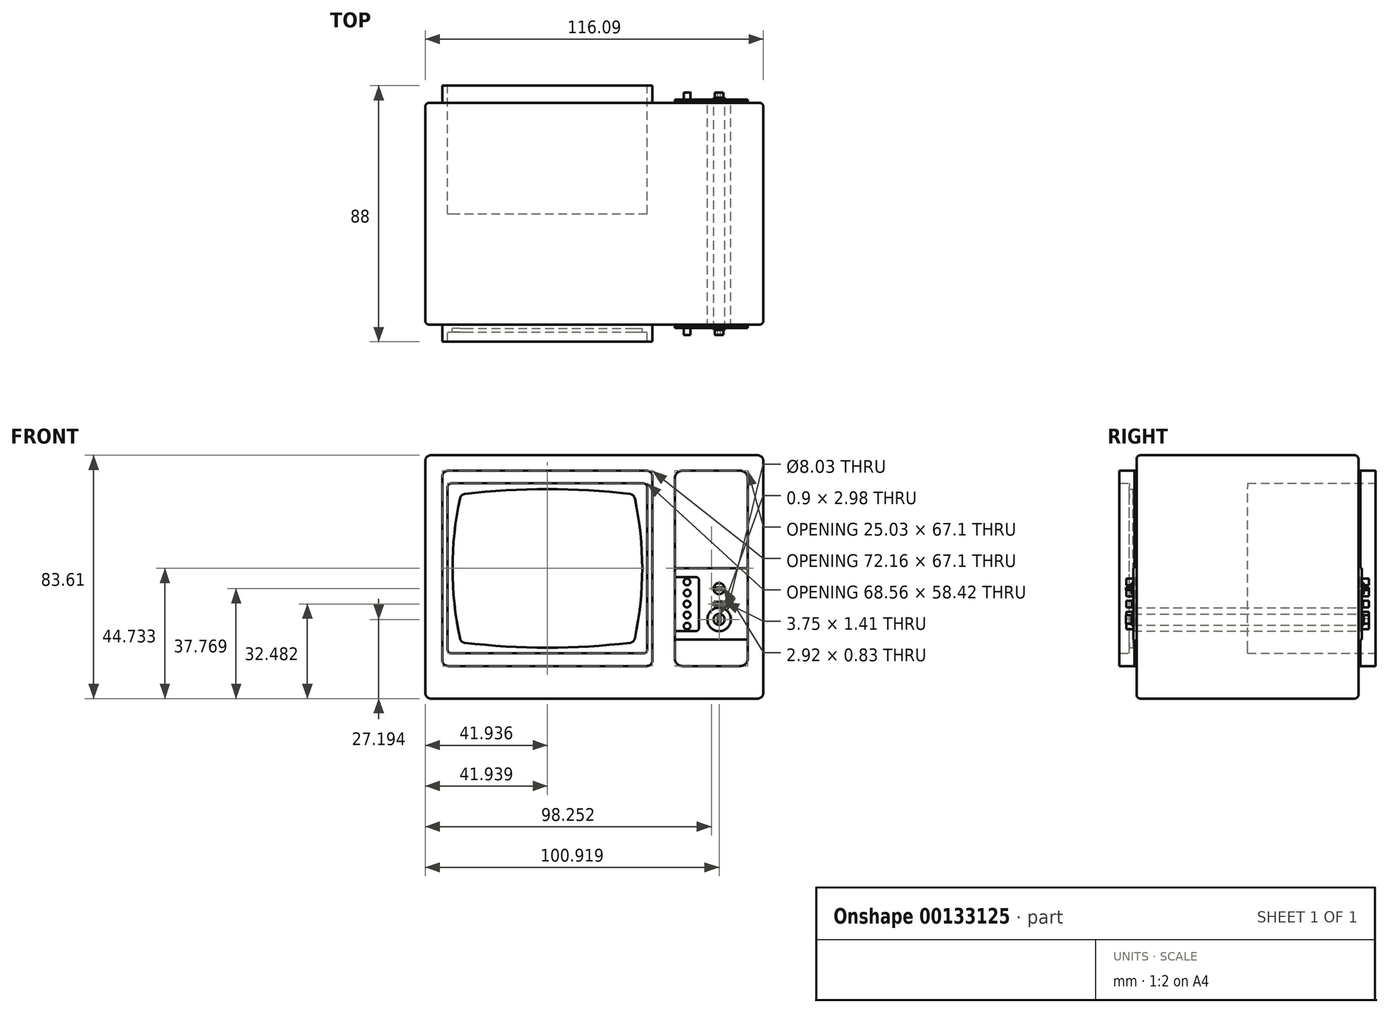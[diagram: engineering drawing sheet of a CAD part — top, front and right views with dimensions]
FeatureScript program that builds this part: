
annotation { "Feature Type Name" : "Feature", "Feature Type Description" : "" }
export const myFeature = defineFeature(function(context is Context, id is Id, definition is map)
    precondition{}
    {
        {
            var Q0;
            Q0=qCreatedBy(makeId("Front.planeOp"),FACE);
            var sketch = newSketch(context, id + "F0", { "sketchPlane" : qUnion([Q0])});
            skLineSegment(sketch, "E0.bottom", {"start": v(-54.54, 43.27) * mm, "end": v(57.74, 43.27) * mm});
            skLineSegment(sketch, "E0.top", {"start": v(-54.54, -40.34) * mm, "end": v(57.74, -40.34) * mm});
            skLineSegment(sketch, "E0.left", {"start": v(-56.45, 41.36) * mm, "end": v(-56.45, -38.43) * mm});
            skLineSegment(sketch, "E0.right", {"start": v(59.64, 41.36) * mm, "end": v(59.64, -38.43) * mm});
            skLineSegment(sketch, "E1.bottom", {"start": v(-48.68, 37.94) * mm, "end": v(19.66, 37.94) * mm});
            skLineSegment(sketch, "E1.top", {"start": v(-48.68, -29.16) * mm, "end": v(19.66, -29.16) * mm});
            skLineSegment(sketch, "E1.left", {"start": v(-50.59, 36.04) * mm, "end": v(-50.59, -27.25) * mm});
            skLineSegment(sketch, "E1.right", {"start": v(21.57, 36.04) * mm, "end": v(21.57, -27.25) * mm});
            skLineSegment(sketch, "E2.bottom", {"start": v(31.83, 37.94) * mm, "end": v(51.78, 37.94) * mm});
            skLineSegment(sketch, "E2.left", {"start": v(29.29, 35.4) * mm, "end": v(29.29, -26.62) * mm});
            skLineSegment(sketch, "E2.right", {"start": v(54.32, 35.4) * mm, "end": v(54.32, -26.62) * mm});
            skPoint(sketch, "E3.visualSharp", {"position": v(54.32, 37.94) * mm});
            skArc(sketch, "E3.filletArc", {"start": v(54.32, 35.4) * mm, "mid": v(53.57, 37.2) * mm, "end": v(51.78, 37.94) * mm});
            skPoint(sketch, "E4.visualSharp", {"position": v(54.32, -29.16) * mm});
            skArc(sketch, "E4.filletArc", {"start": v(51.78, -29.16) * mm, "mid": v(53.57, -28.41) * mm, "end": v(54.32, -26.62) * mm});
            skPoint(sketch, "E5.visualSharp", {"position": v(29.29, 37.94) * mm});
            skArc(sketch, "E5.filletArc", {"start": v(31.83, 37.94) * mm, "mid": v(30.03, 37.2) * mm, "end": v(29.29, 35.4) * mm});
            skPoint(sketch, "E6.visualSharp", {"position": v(29.29, -29.16) * mm});
            skArc(sketch, "E6.filletArc", {"start": v(29.29, -26.62) * mm, "mid": v(30.03, -28.41) * mm, "end": v(31.83, -29.16) * mm});
            skLineSegment(sketch, "E7", {"start": v(29.29, 4.4) * mm, "end": v(54.32, 4.4) * mm});
            skLineSegment(sketch, "E8", {"start": v(29.29, -20.1) * mm, "end": v(54.32, -20.1) * mm});
            skLineSegment(sketch, "E9", {"start": v(29.29, 1.46) * mm, "end": v(34.62, 1.46) * mm});
            skLineSegment(sketch, "E10", {"start": v(29.29, -17.18) * mm, "end": v(34.62, -17.18) * mm});
            skCircle(sketch, "E11", {"center": v(44.47, -2.57) * mm, "radius": 4.02 * mm});
            skCircle(sketch, "E12.MirrorC", {"center": v(44.47, -13.15) * mm, "radius": 4.02 * mm});
            skLineSegment(sketch, "E13", {"start": v(34.62, 1.46) * mm, "end": v(36.34, 1.46) * mm});
            skLineSegment(sketch, "E14", {"start": v(37.6, 0.2) * mm, "end": v(37.6, -15.92) * mm});
            skLineSegment(sketch, "E15", {"start": v(36.34, -17.18) * mm, "end": v(34.62, -17.18) * mm});
            skLineSegment(sketch, "E16", {"start": v(29.29, 1.46) * mm, "end": v(29.29, -17.18) * mm});
            skLineSegment(sketch, "E17", {"start": v(29.29, -7.86) * mm, "end": v(29.29, 1.46) * mm});
            skLineSegment(sketch, "E18", {"start": v(29.29, -7.86) * mm, "end": v(29.29, -17.18) * mm});
            skLineSegment(sketch, "E19.bottom", {"start": v(46.35, -7.15) * mm, "end": v(42.6, -7.15) * mm});
            skLineSegment(sketch, "E19.top", {"start": v(46.35, -8.56) * mm, "end": v(42.6, -8.56) * mm});
            skLineSegment(sketch, "E19.left", {"start": v(46.35, -7.15) * mm, "end": v(46.35, -8.56) * mm});
            skLineSegment(sketch, "E19.right", {"start": v(42.6, -7.15) * mm, "end": v(42.6, -8.56) * mm});
            skPoint(sketch, "E19.middle", {"position": v(44.47, -7.86) * mm});
            skCircle(sketch, "E20", {"center": v(33.44, -7.86) * mm, "radius": 1.14 * mm});
            skCircle(sketch, "E21", {"center": v(33.44, -0.3) * mm, "radius": 1.14 * mm});
            skCircle(sketch, "E22", {"center": v(33.47, -15.42) * mm, "radius": 1.14 * mm});
            skCircle(sketch, "E23", {"center": v(33.52, -4.08) * mm, "radius": 1.15 * mm});
            skCircle(sketch, "E24", {"center": v(33.47, -11.64) * mm, "radius": 1.15 * mm});
            skPoint(sketch, "E25.endSnap0", {"position": v(-50.59, 4.4) * mm});
            skArc(sketch, "E26", {"start": v(13.87, 29.96) * mm, "mid": v(-14.51, 31.63) * mm, "end": v(-42.9, 29.96) * mm});
            skArc(sketch, "E27", {"start": v(-42.9, -21.17) * mm, "mid": v(-14.51, -22.84) * mm, "end": v(13.87, -21.17) * mm});
            skArc(sketch, "E28", {"start": v(-44.53, 28.47) * mm, "mid": v(-47.1, 4.4) * mm, "end": v(-44.53, -19.68) * mm});
            skArc(sketch, "E29", {"start": v(15.51, -19.68) * mm, "mid": v(18.07, 4.4) * mm, "end": v(15.51, 28.47) * mm});
            skPoint(sketch, "E30.visualSharp", {"position": v(21.57, 37.94) * mm});
            skArc(sketch, "E30.filletArc", {"start": v(21.57, 36.04) * mm, "mid": v(21, 37.38) * mm, "end": v(19.66, 37.94) * mm});
            skPoint(sketch, "E31.visualSharp", {"position": v(-50.59, 37.94) * mm});
            skArc(sketch, "E31.filletArc", {"start": v(-48.68, 37.94) * mm, "mid": v(-50.03, 37.38) * mm, "end": v(-50.59, 36.04) * mm});
            skPoint(sketch, "E32.visualSharp", {"position": v(-50.59, -29.16) * mm});
            skArc(sketch, "E32.filletArc", {"start": v(-50.59, -27.25) * mm, "mid": v(-50.03, -28.6) * mm, "end": v(-48.68, -29.16) * mm});
            skPoint(sketch, "E33.visualSharp", {"position": v(21.57, -29.16) * mm});
            skArc(sketch, "E33.filletArc", {"start": v(19.66, -29.16) * mm, "mid": v(21, -28.6) * mm, "end": v(21.57, -27.25) * mm});
            skPoint(sketch, "E34.visualSharp", {"position": v(-44.24, 29.8) * mm});
            skArc(sketch, "E34.filletArc", {"start": v(-42.9, 29.96) * mm, "mid": v(-43.95, 29.47) * mm, "end": v(-44.53, 28.47) * mm});
            skPoint(sketch, "E35.visualSharp", {"position": v(15.22, 29.8) * mm});
            skArc(sketch, "E35.filletArc", {"start": v(15.51, 28.47) * mm, "mid": v(14.93, 29.47) * mm, "end": v(13.87, 29.96) * mm});
            skPoint(sketch, "E36.visualSharp", {"position": v(15.22, -21) * mm});
            skArc(sketch, "E36.filletArc", {"start": v(13.87, -21.17) * mm, "mid": v(14.93, -20.69) * mm, "end": v(15.51, -19.68) * mm});
            skPoint(sketch, "E37.visualSharp", {"position": v(-44.24, -21) * mm});
            skArc(sketch, "E37.filletArc", {"start": v(-44.53, -19.68) * mm, "mid": v(-43.95, -20.69) * mm, "end": v(-42.9, -21.17) * mm});
            skPoint(sketch, "E38.visualSharp", {"position": v(-56.45, 43.27) * mm});
            skArc(sketch, "E38.filletArc", {"start": v(-54.54, 43.27) * mm, "mid": v(-55.89, 42.7) * mm, "end": v(-56.45, 41.36) * mm});
            skPoint(sketch, "E39.visualSharp", {"position": v(-56.45, -40.34) * mm});
            skArc(sketch, "E39.filletArc", {"start": v(-56.45, -38.43) * mm, "mid": v(-55.89, -39.78) * mm, "end": v(-54.54, -40.34) * mm});
            skPoint(sketch, "E40.visualSharp", {"position": v(59.64, -40.34) * mm});
            skArc(sketch, "E40.filletArc", {"start": v(57.74, -40.34) * mm, "mid": v(59.08, -39.78) * mm, "end": v(59.64, -38.43) * mm});
            skPoint(sketch, "E41.visualSharp", {"position": v(59.64, 43.27) * mm});
            skArc(sketch, "E41.filletArc", {"start": v(59.64, 41.36) * mm, "mid": v(59.08, 42.7) * mm, "end": v(57.74, 43.27) * mm});
            skPoint(sketch, "E42.visualSharp", {"position": v(37.6, -17.18) * mm});
            skArc(sketch, "E42.filletArc", {"start": v(36.34, -17.18) * mm, "mid": v(37.23, -16.81) * mm, "end": v(37.6, -15.92) * mm});
            skPoint(sketch, "E43.visualSharp", {"position": v(37.6, 1.46) * mm});
            skArc(sketch, "E43.filletArc", {"start": v(37.6, 0.2) * mm, "mid": v(37.23, 1.1) * mm, "end": v(36.34, 1.46) * mm});
            skLineSegment(sketch, "E44", {"start": v(-50.59, 4.4) * mm, "end": v(-47, 4.4) * mm});
            skLineSegment(sketch, "E45", {"start": v(-48.8, 4.4) * mm, "end": v(-48.8, -23.56) * mm});
            skLineSegment(sketch, "E46", {"start": v(-48.8, 4.4) * mm, "end": v(-48.8, 32.35) * mm});
            skLineSegment(sketch, "E47", {"start": v(21.57, 4.4) * mm, "end": v(17.96, 4.4) * mm});
            skLineSegment(sketch, "E48", {"start": v(19.76, 4.4) * mm, "end": v(19.76, 32.35) * mm});
            skLineSegment(sketch, "E49", {"start": v(19.76, 4.4) * mm, "end": v(19.76, -23.56) * mm});
            skLineSegment(sketch, "E50", {"start": v(-47.54, 33.6) * mm, "end": v(18.5, 33.6) * mm});
            skLineSegment(sketch, "E51", {"start": v(-47.54, -24.82) * mm, "end": v(18.5, -24.82) * mm});
            skPoint(sketch, "E52.visualSharp", {"position": v(-48.8, 33.6) * mm});
            skArc(sketch, "E52.filletArc", {"start": v(-47.54, 33.6) * mm, "mid": v(-48.42, 33.24) * mm, "end": v(-48.8, 32.35) * mm});
            skPoint(sketch, "E53.visualSharp", {"position": v(19.76, 33.6) * mm});
            skArc(sketch, "E53.filletArc", {"start": v(19.76, 32.35) * mm, "mid": v(19.4, 33.24) * mm, "end": v(18.5, 33.6) * mm});
            skPoint(sketch, "E54.visualSharp", {"position": v(19.76, -24.82) * mm});
            skArc(sketch, "E54.filletArc", {"start": v(18.5, -24.82) * mm, "mid": v(19.4, -24.45) * mm, "end": v(19.76, -23.56) * mm});
            skPoint(sketch, "E55.visualSharp", {"position": v(-48.8, -24.82) * mm});
            skArc(sketch, "E55.filletArc", {"start": v(-48.8, -23.56) * mm, "mid": v(-48.42, -24.45) * mm, "end": v(-47.54, -24.82) * mm});
            skLineSegment(sketch, "E56", {"start": v(51.78, -29.16) * mm, "end": v(31.83, -29.16) * mm});
            skCircle(sketch, "E57", {"center": v(44.47, -2.57) * mm, "radius": 1.9 * mm});
            skCircle(sketch, "E58", {"center": v(44.47, -13.15) * mm, "radius": 1.9 * mm});
            skLineSegment(sketch, "E59.bottom", {"start": v(44.02, -11.65) * mm, "end": v(44.92, -11.65) * mm});
            skLineSegment(sketch, "E59.top", {"start": v(44.02, -14.64) * mm, "end": v(44.92, -14.64) * mm});
            skLineSegment(sketch, "E59.left", {"start": v(44.02, -11.65) * mm, "end": v(44.02, -14.64) * mm});
            skLineSegment(sketch, "E59.right", {"start": v(44.92, -11.65) * mm, "end": v(44.92, -14.64) * mm});
            skLineSegment(sketch, "E60.bottom", {"start": v(45.93, -2.15) * mm, "end": v(43, -2.15) * mm});
            skLineSegment(sketch, "E60.top", {"start": v(45.93, -2.99) * mm, "end": v(43, -2.99) * mm});
            skLineSegment(sketch, "E60.left", {"start": v(45.93, -2.15) * mm, "end": v(45.93, -2.99) * mm});
            skLineSegment(sketch, "E60.right", {"start": v(43, -2.15) * mm, "end": v(43, -2.99) * mm});
            skSolve(sketch);
        }
        {
            var Q0;
            Q0 = qSketchRegion(id + "F0", true);
            extrude(context, id + "F1", {"entities" : qUnion([Q0]), "endBound" : BoundingType.SYMMETRIC, "depth" : 76.2 * mm});
        }
        {
            var Q0;
            Q0=makeQuery(id+"F0.imprint","IMPRINT",FACE,{"disambiguationData":[TD([[makeQuery(id+"F0.imprint","IMPRINT",EDGE,{"derivedFrom":sQuery(id+"F0.wireOp",EDGE,"E1.bottom")}),-1.0]])]});
            var Q1;
            Q1=makeQuery(id+"F0.imprint","IMPRINT",FACE,{"disambiguationData":[TD([[makeQuery(id+"F0.imprint","IMPRINT",EDGE,{"derivedFrom":sQuery(id+"F0.wireOp",EDGE,"E1.top")}),1.0]])]});
            extrude(context, id + "F2", {"entities" : qUnion([Q0, Q1]), "operationType" : NewBodyOperationType.ADD, "endBound" : BoundingType.SYMMETRIC, "depth" : 88 * mm});
        }
        {
            var Q0;
            Q0=makeQuery(id+"F0.imprint","IMPRINT",FACE,{"disambiguationData":[TD([[makeQuery(id+"F0.imprint","IMPRINT",EDGE,{"derivedFrom":sQuery(id+"F0.wireOp",EDGE,"E26")}),-1.0]])]});
            var Q1;
            Q1=makeQuery(id+"F0.imprint","IMPRINT",FACE,{"disambiguationData":[TD([[makeQuery(id+"F0.imprint","IMPRINT",EDGE,{"derivedFrom":sQuery(id+"F0.wireOp",EDGE,"E27")}),-1.0]])]});
            extrude(context, id + "F3", {"entities" : qUnion([Q0, Q1]), "operationType" : NewBodyOperationType.ADD, "depth" : 40.64 * mm});
        }
        {
            var Q0;
            Q0=makeQuery(id+"F0.imprint","IMPRINT",FACE,{"disambiguationData":[TD([[makeQuery(id+"F0.imprint","IMPRINT",EDGE,{"derivedFrom":sQuery(id+"F0.wireOp",EDGE,"E26")}),1.0]])]});
            extrude(context, id + "F4", {"entities" : qUnion([Q0]), "operationType" : NewBodyOperationType.ADD, "depth" : 39.37 * mm});
        }
        {
            var Q0;
            Q0=makeQuery(id+"F0.imprint","IMPRINT",FACE,{"disambiguationData":[TD([[makeQuery(id+"F0.imprint","IMPRINT",EDGE,{"derivedFrom":sQuery(id+"F0.wireOp",EDGE,"E2.bottom")}),-1.0]])]});
            var Q1;
            {var subQ1=sQuery(id+"F0.wireOp",EDGE,"E4.filletArc");Q1=makeQuery(id+"F0.imprint","IMPRINT",FACE,{"disambiguationData":[TD([[makeQuery(id+"F0.imprint","IMPRINT",EDGE,{"derivedFrom":subQ1}),1.0]])]});}
            var Q2;
            {var subQ4=sQuery(id+"F0.wireOp",EDGE,"E7");Q2=makeQuery(id+"F0.imprint","IMPRINT",FACE,{"disambiguationData":[TD([[makeQuery(id+"F0.imprint","IMPRINT",EDGE,{"derivedFrom":subQ4}),-1.0]])]});}
            var Q3;
            Q3=makeQuery(id+"F0.imprint","IMPRINT",FACE,{"disambiguationData":[TD([[makeQuery(id+"F0.imprint","IMPRINT",EDGE,{"derivedFrom":sQuery(id+"F0.wireOp",EDGE,"E9")}),-1.0]])]});
            extrude(context, id + "F5", {"entities" : qUnion([Q0, Q1, Q2, Q3]), "operationType" : NewBodyOperationType.ADD, "endBound" : BoundingType.SYMMETRIC, "depth" : 77.6 * mm});
        }
        {
            var Q0;
            Q0=makeQuery(id+"F0.imprint","IMPRINT",FACE,{"disambiguationData":[TD([[makeQuery(id+"F0.imprint","IMPRINT",EDGE,{"derivedFrom":sQuery(id+"F0.wireOp",EDGE,"E19.bottom")}),1.0]])]});
            extrude(context, id + "F6", {"entities" : qUnion([Q0]), "operationType" : NewBodyOperationType.ADD, "endBound" : BoundingType.SYMMETRIC, "depth" : 79.28 * mm});
        }
        {
            var Q0;
            Q0=makeQuery(id+"F0.imprint","IMPRINT",FACE,{"disambiguationData":[TD([[makeQuery(id+"F0.imprint","IMPRINT",EDGE,{"derivedFrom":sQuery(id+"F0.wireOp",EDGE,"E21")}),1.0]])]});
            var Q1;
            Q1=makeQuery(id+"F0.imprint","IMPRINT",FACE,{"disambiguationData":[TD([[makeQuery(id+"F0.imprint","IMPRINT",EDGE,{"derivedFrom":sQuery(id+"F0.wireOp",EDGE,"E23")}),1.0]])]});
            var Q2;
            Q2=makeQuery(id+"F0.imprint","IMPRINT",FACE,{"disambiguationData":[TD([[makeQuery(id+"F0.imprint","IMPRINT",EDGE,{"derivedFrom":sQuery(id+"F0.wireOp",EDGE,"E20")}),1.0]])]});
            var Q3;
            Q3=makeQuery(id+"F0.imprint","IMPRINT",FACE,{"disambiguationData":[TD([[makeQuery(id+"F0.imprint","IMPRINT",EDGE,{"derivedFrom":sQuery(id+"F0.wireOp",EDGE,"E24")}),1.0]])]});
            var Q4;
            Q4=makeQuery(id+"F0.imprint","IMPRINT",FACE,{"disambiguationData":[TD([[makeQuery(id+"F0.imprint","IMPRINT",EDGE,{"derivedFrom":sQuery(id+"F0.wireOp",EDGE,"E22")}),1.0]])]});
            extrude(context, id + "F7", {"entities" : qUnion([Q0, Q1, Q2, Q3, Q4]), "operationType" : NewBodyOperationType.ADD, "endBound" : BoundingType.SYMMETRIC, "depth" : 83.3 * mm});
        }
        {
            var Q0;
            Q0=makeQuery(id+"F0.imprint","IMPRINT",FACE,{"disambiguationData":[TD([[makeQuery(id+"F0.imprint","IMPRINT",EDGE,{"derivedFrom":sQuery(id+"F0.wireOp",EDGE,"E11")}),1.0]])]});
            var Q1;
            Q1=makeQuery(id+"F0.imprint","IMPRINT",FACE,{"disambiguationData":[TD([[makeQuery(id+"F0.imprint","IMPRINT",EDGE,{"derivedFrom":sQuery(id+"F0.wireOp",EDGE,"E12.MirrorC")}),-1.0]])]});
            extrude(context, id + "F8", {"entities" : qUnion([Q0, Q1]), "operationType" : NewBodyOperationType.ADD, "endBound" : BoundingType.SYMMETRIC, "depth" : 78.49 * mm});
        }
        {
            var Q0;
            Q0=makeQuery(id+"F0.imprint","IMPRINT",FACE,{"disambiguationData":[TD([[makeQuery(id+"F0.imprint","IMPRINT",EDGE,{"derivedFrom":sQuery(id+"F0.wireOp",EDGE,"E57")}),1.0]])]});
            var Q1;
            Q1=makeQuery(id+"F0.imprint","IMPRINT",FACE,{"disambiguationData":[TD([[makeQuery(id+"F0.imprint","IMPRINT",EDGE,{"derivedFrom":sQuery(id+"F0.wireOp",EDGE,"E58")}),1.0]])]});
            extrude(context, id + "F9", {"entities" : qUnion([Q0, Q1]), "operationType" : NewBodyOperationType.ADD, "endBound" : BoundingType.SYMMETRIC, "depth" : 79.78 * mm});
        }
        {
            var Q0;
            Q0=makeQuery(id+"F0.imprint","IMPRINT",FACE,{"disambiguationData":[TD([[makeQuery(id+"F0.imprint","IMPRINT",EDGE,{"derivedFrom":sQuery(id+"F0.wireOp",EDGE,"E59.bottom")}),-1.0]])]});
            var Q1;
            Q1=makeQuery(id+"F0.imprint","IMPRINT",FACE,{"disambiguationData":[TD([[makeQuery(id+"F0.imprint","IMPRINT",EDGE,{"derivedFrom":sQuery(id+"F0.wireOp",EDGE,"E60.bottom")}),1.0]])]});
            extrude(context, id + "F10", {"entities" : qUnion([Q0, Q1]), "operationType" : NewBodyOperationType.ADD, "endBound" : BoundingType.SYMMETRIC, "depth" : 83.33 * mm});
        }
        {
            var Q0;
            Q0=makeQuery(id+"F1.opExtrude","SWEPT_FACE",FACE,{"disambiguationData":[OSD([sQuery(id+"F0.wireOp",EDGE,"E0.bottom")])]});
            var Q1;
            Q1=makeQuery(id+"F1.opExtrude","SWEPT_FACE",FACE,{"disambiguationData":[OSD([sQuery(id+"F0.wireOp",EDGE,"E0.right")])]});
            var Q2;
            Q2=makeQuery(id+"F1.opExtrude","SWEPT_FACE",FACE,{"disambiguationData":[OSD([sQuery(id+"F0.wireOp",EDGE,"E41.filletArc")])]});
            var Q3;
            Q3=makeQuery(id+"F1.opExtrude","SWEPT_FACE",FACE,{"disambiguationData":[OSD([sQuery(id+"F0.wireOp",EDGE,"E0.top")])]});
            var Q4;
            Q4=makeQuery(id+"F1.opExtrude","SWEPT_FACE",FACE,{"disambiguationData":[OSD([sQuery(id+"F0.wireOp",EDGE,"E40.filletArc")])]});
            var Q5;
            Q5=makeQuery(id+"F1.opExtrude","SWEPT_FACE",FACE,{"disambiguationData":[OSD([sQuery(id+"F0.wireOp",EDGE,"E0.left")])]});
            var Q6;
            Q6=makeQuery(id+"F1.opExtrude","SWEPT_FACE",FACE,{"disambiguationData":[OSD([sQuery(id+"F0.wireOp",EDGE,"E39.filletArc")])]});
            var Q7;
            Q7=makeQuery(id+"F1.opExtrude","SWEPT_FACE",FACE,{"disambiguationData":[OSD([sQuery(id+"F0.wireOp",EDGE,"E38.filletArc")])]});
            fillet(context, id + "F11", {"entities" : qUnion([Q0, Q1, Q2, Q3, Q4, Q5, Q6, Q7]), "radius" : 1.27 * mm, "tangentPropagation" : true, "allowEdgeOverflow" : false});
        }
    });
